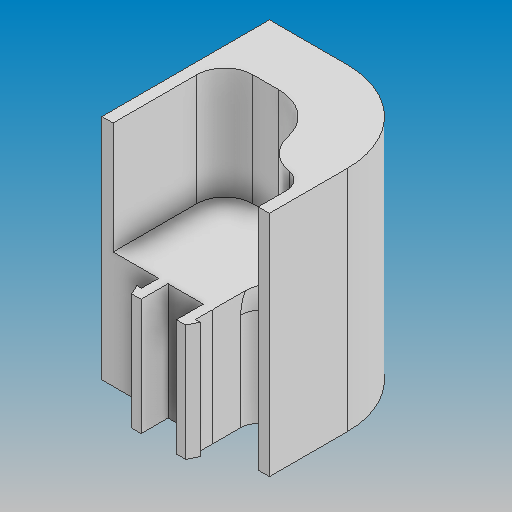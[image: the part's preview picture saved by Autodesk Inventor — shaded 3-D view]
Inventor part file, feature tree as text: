
AUTODESK INVENTOR PART (.ipt)
format: ipt  version: 2021 (Build 250183000, 183)  size: 172,544 bytes
history: native  units: mm
features: other x3, extrude x1, sketch x1
ambient origin geometry x8: Origin, YZ Plane, XZ Plane, XY Plane, X Axis, Y Axis, Z Axis, Center Point
bodies: Volumenkörper1 (feature_tree)
feature tree (5):
  other  "Corner1.ipt"
  extrude  "Extrusion1"  Depth=10.0mm
  other  "Volumenkörper1::Corner1.ipt"
  other  "Bezeichnung1"
  sketch  "Skizze1"  dims[d0=10.0mm d1=10.0mm d2=0.0mm d3=0.0mm]
